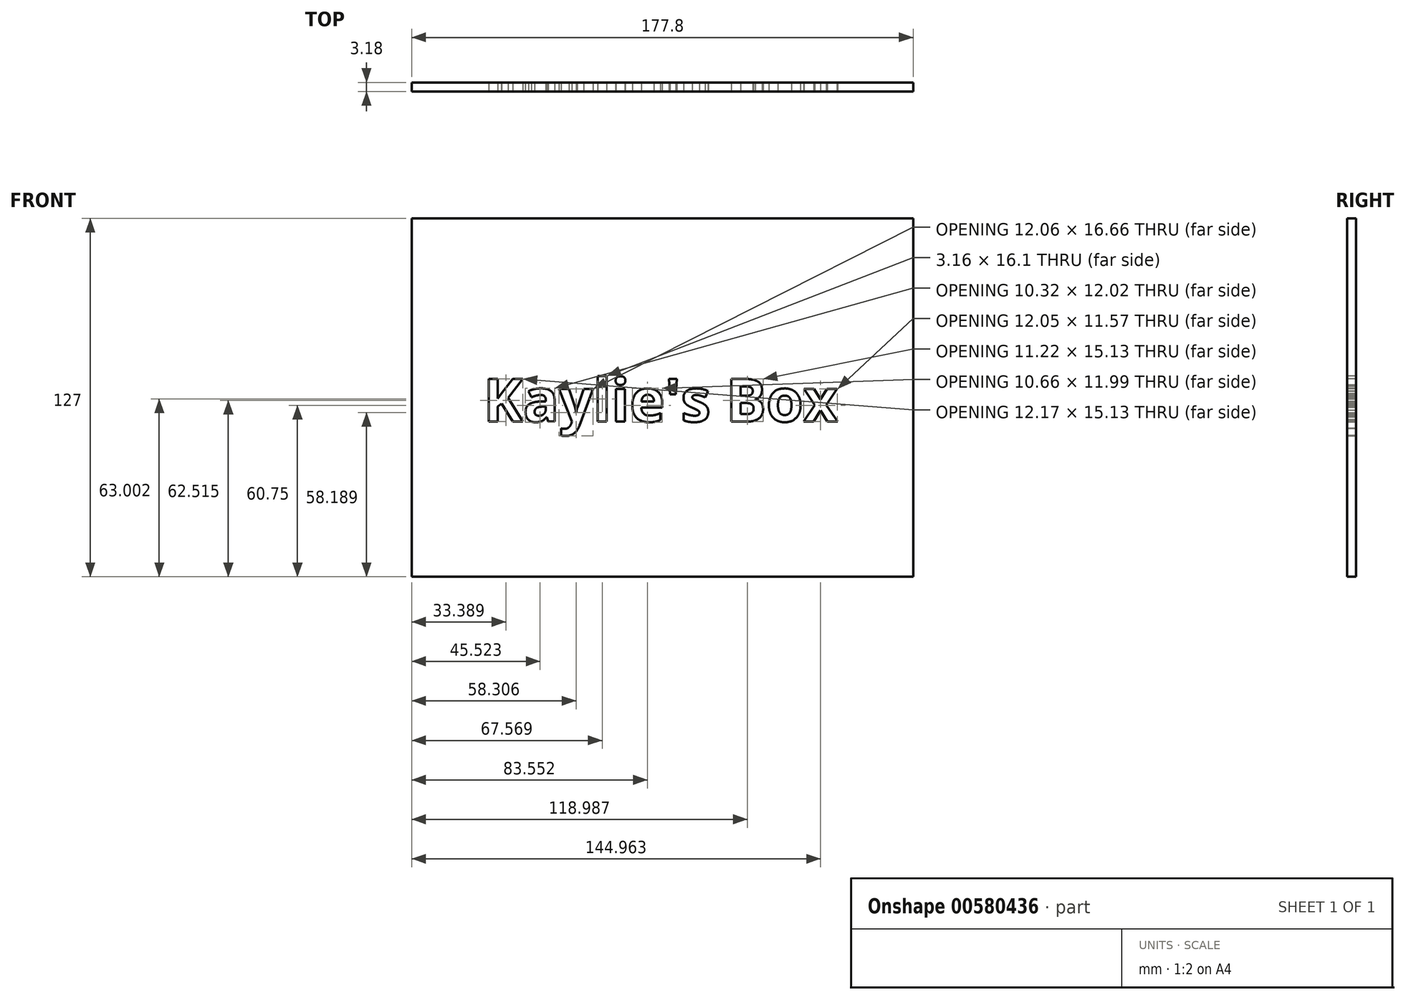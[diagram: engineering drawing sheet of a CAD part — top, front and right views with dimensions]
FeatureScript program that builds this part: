
annotation { "Feature Type Name" : "Feature", "Feature Type Description" : "" }
export const myFeature = defineFeature(function(context is Context, id is Id, definition is map)
    precondition{}
    {
        {
            var Q0;
            Q0=qCreatedBy(makeId("Front.planeOp"),FACE);
            var sketch = newSketch(context, id + "F0", { "sketchPlane" : qUnion([Q0])});
            skLineSegment(sketch, "E0.bottom", {"start": v(-147.88, 103.38) * mm, "end": v(29.92, 103.38) * mm});
            skLineSegment(sketch, "E0.top", {"start": v(-147.88, -23.62) * mm, "end": v(29.92, -23.62) * mm});
            skLineSegment(sketch, "E0.left", {"start": v(-147.88, 103.38) * mm, "end": v(-147.88, -23.62) * mm});
            skLineSegment(sketch, "E0.right", {"start": v(29.92, 103.38) * mm, "end": v(29.92, -23.62) * mm});
            skSolve(sketch);
        }
        {
            var Q0;
            Q0 = qSketchRegion(id + "F0", true);
            extrude(context, id + "F1", {"entities" : qUnion([Q0]), "depth" : 3.17 * mm, "offsetDistance" : 25.4 * mm});
        }
        {
            var Q0;
            Q0=makeQuery(id+"F1.opExtrude","CAP_FACE",FACE,{"disambiguationData":[OSD([sQuery(id+"F0.wireOp",EDGE,"E0.bottom"),sQuery(id+"F0.wireOp",EDGE,"E0.top"),sQuery(id+"F0.wireOp",EDGE,"E0.left"),sQuery(id+"F0.wireOp",EDGE,"E0.right")])],"isStart":false});
            var sketch = newSketch(context, id + "F2", { "sketchPlane" : qUnion([Q0])});
            skText(sketch, "E1", { "text": "Kaylie\'s Box", "fontName": "OpenSans-Bold.ttf"});
            const initialGuessF2  = {"E1": [-0.12248, 0.03133, 1, 0, 0.01526]};
            skSetInitialGuess(sketch, initialGuessF2);
            skSolve(sketch);
        }
        {
            var Q0;
            Q0 = qSketchRegion(id + "F2", true);
            extrude(context, id + "F3", {"entities" : qUnion([Q0]), "operationType" : NewBodyOperationType.REMOVE, "oppositeDirection" : true, "depth" : 25.4 * mm, "offsetDistance" : 25.4 * mm});
        }
    });
